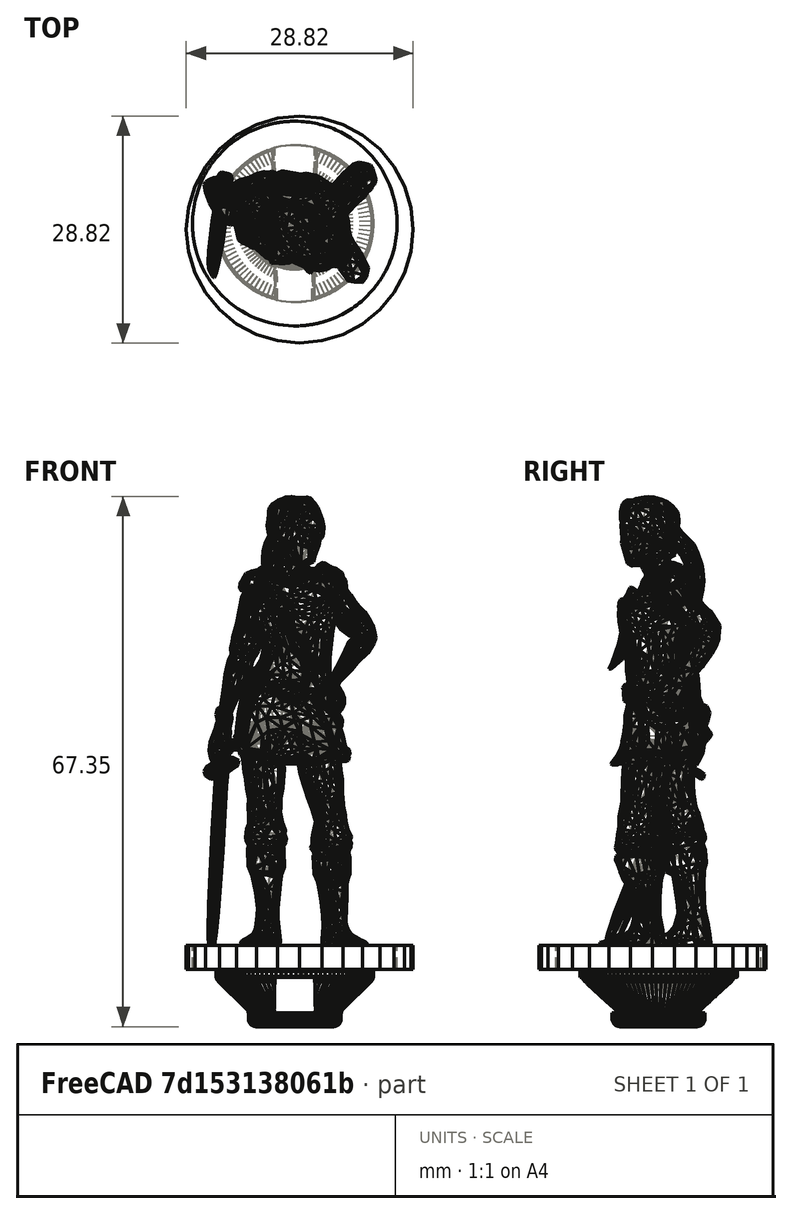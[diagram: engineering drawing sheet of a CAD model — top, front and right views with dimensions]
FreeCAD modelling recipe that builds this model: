
FCSTD DOCUMENT  (FreeCAD 0.17R13541 (Git))
Label: SR4base27
License: All rights reserved
LicenseURL: http://en.wikipedia.org/wiki/All_rights_reserved
objects: Part::Feature×5, Mesh::Feature×2, Part::Cylinder×2, Part::Cut×2, Part::Fuse×1
note: 10 computed .brp shape members not serialized (recipe doc carries the construction recipe); baked Part::Feature solids carry a one-line shape summary decoded from their .brp

FEATURE [Mesh::Feature] FemaleKnight_StandRelaxed_Cleaned4
FEATURE [Part::Feature] FemaleKnight_StandRelaxed_Cleaned4001
  shape: bbox 28.82 x 28.82 x 60.05 mm, 8000 faces, 0 solids (baked)
FEATURE [Part::Feature] FemaleKnight_StandRelaxed_Cleaned4001_solid  label="FemaleKnight_StandRelaxed_Cleaned4001 (Solid)"
  shape: bbox 28.82 x 28.82 x 60.05 mm, 8000 faces (baked)
FEATURE [Part::Cylinder] Cylinder001
  Angle = 360
  AttacherType = Attacher::AttachEngine3D
  Height = 7
  Radius = 13
FEATURE [Part::Cylinder] Cylinder002
  Angle = 360
  AttacherType = Attacher::AttachEngine3D
  Height = 7
  Radius = 16
FEATURE [Part::Cut] Cut
  Base = -> Cylinder002
  Tool = -> Cylinder001
FEATURE [Part::Cut] Cut001
  Base = -> FemaleKnight_StandRelaxed_Cleaned4001_solid
  Tool = -> Cut
FEATURE [Mesh::Feature] Base27
  Placement = pos=(0,0,-7) rot=(0,0,1;0rad)
FEATURE [Part::Feature] Base27001
  shape: bbox 19.99 x 20 x 8 mm, 15618 faces, 0 solids (baked)
FEATURE [Part::Feature] Base27001_solid  label="Base27001 (Solid)"
  shape: bbox 19.99 x 20 x 8 mm, 15618 faces (baked)
FEATURE [Part::Feature] FemaleKnight_StandRelaxed_Cleaned4001_solid001  label="FemaleKnight_StandRelaxed_Cleaned4001 (Solid)001"
  shape: bbox 28.82 x 28.82 x 60.05 mm, 8000 faces (baked)
FEATURE [Part::Fuse] Fusion
  Base = -> Base27001_solid
  Tool = -> FemaleKnight_StandRelaxed_Cleaned4001_solid001
